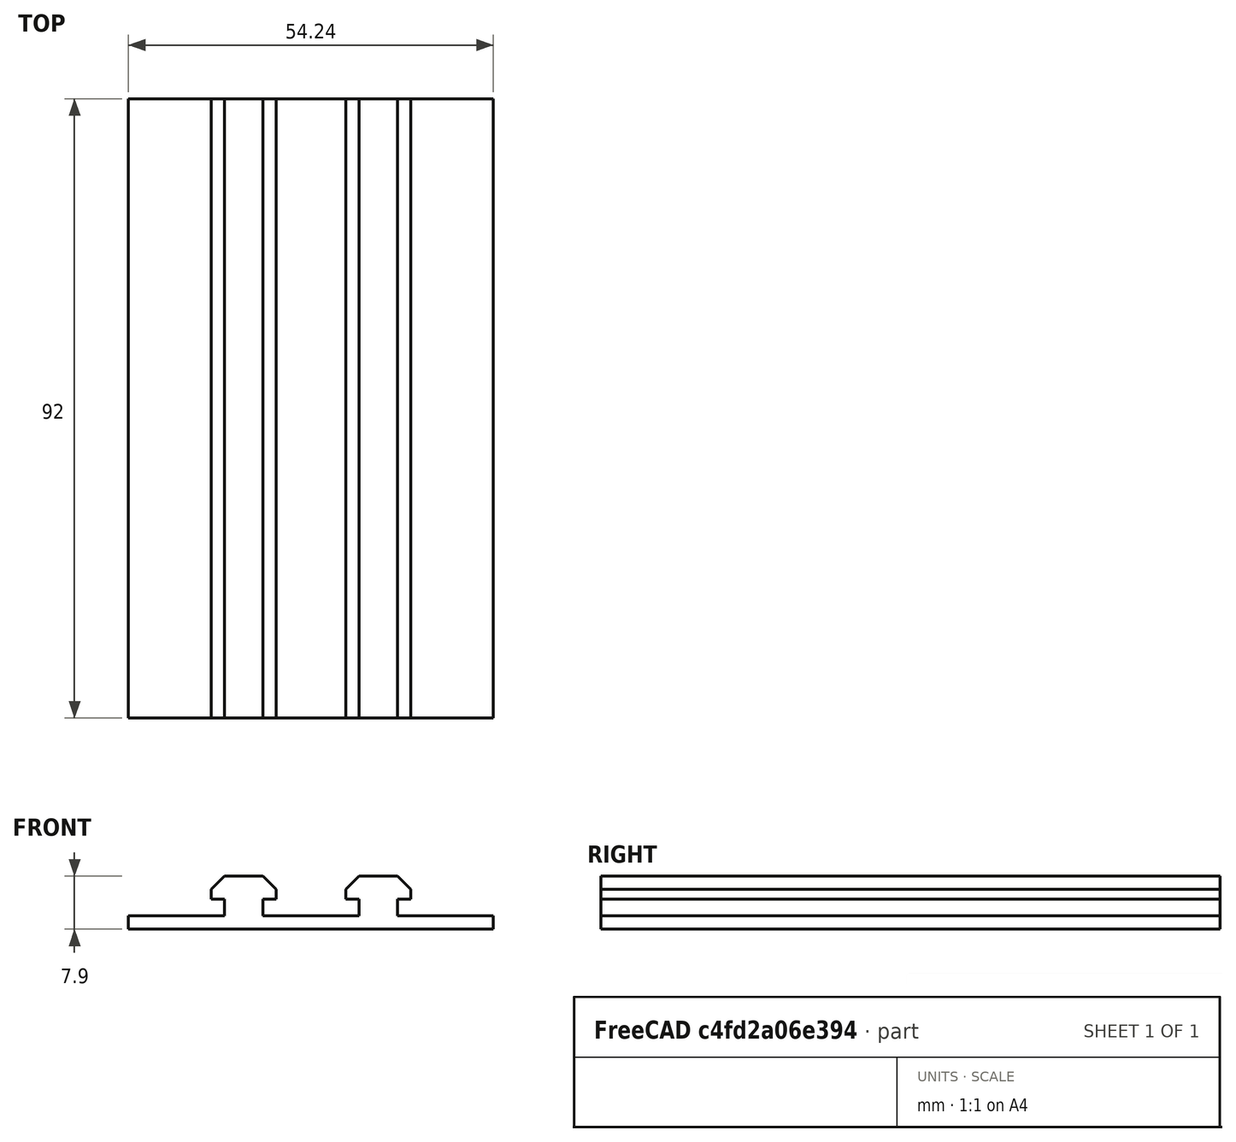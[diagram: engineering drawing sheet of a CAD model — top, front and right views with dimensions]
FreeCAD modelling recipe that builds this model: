
FCSTD DOCUMENT  (FreeCAD 1.0R39109 (Git))
Label: 04 Base Attachment
License: All rights reserved
LicenseURL: https://en.wikipedia.org/wiki/All_rights_reserved
objects: Sketcher::SketchObject×2, PartDesign::Pad×1, PartDesign::Body×1
note: 8 computed .brp shape members not serialized (recipe doc carries the construction recipe); baked Part::Feature solids carry a one-line shape summary decoded from their .brp

FEATURE [Sketcher::SketchObject] Sketch
  ArcFitTolerance = 1e-06
  AttachmentSupport = -> [XZ_Plane]
  FullyConstrained = true
  MakeInternals = false
  MapMode = 5
  Placement = pos=(0,0,0) rot=(1,0,0;1.5708rad)
  sketch-geometry (26):
    g0: LineSegment StartX=-27.12 StartY=0 StartZ=0 EndX=27.12 EndY=0 EndZ=0
    g1: LineSegment StartX=27.12 StartY=0 StartZ=0 EndX=27.12 EndY=2 EndZ=0
    g2: LineSegment StartX=27.12 StartY=2 StartZ=0 EndX=-27.12 EndY=2 EndZ=0
    g3: LineSegment StartX=-27.12 StartY=2 StartZ=0 EndX=-27.12 EndY=0 EndZ=0
    g4: LineSegment StartX=-12.88 StartY=4.5 StartZ=0 EndX=-12.88 EndY=2 EndZ=0
    g5: LineSegment StartX=-12.88 StartY=2 StartZ=0 EndX=-7.12 EndY=2 EndZ=0
    g6: LineSegment StartX=-7.12 StartY=2 StartZ=0 EndX=-7.12 EndY=4.5 EndZ=0
    g7: LineSegment StartX=-7.12 StartY=4.5 StartZ=0 EndX=-12.88 EndY=4.5 EndZ=0
    g8: LineSegment StartX=7.12 StartY=4.5 StartZ=0 EndX=7.12 EndY=2 EndZ=0
    g9: LineSegment StartX=7.12 StartY=2 StartZ=0 EndX=12.88 EndY=2 EndZ=0
    g10: LineSegment StartX=12.88 StartY=2 StartZ=0 EndX=12.88 EndY=4.5 EndZ=0
    g11: LineSegment StartX=12.88 StartY=4.5 StartZ=0 EndX=7.12 EndY=4.5 EndZ=0
    g12: LineSegment StartX=-14.81 StartY=5.93 StartZ=0 EndX=-14.81 EndY=4.5 EndZ=0
    g13: LineSegment StartX=-14.81 StartY=4.5 StartZ=0 EndX=-5.19 EndY=4.5 EndZ=0
    g14: LineSegment StartX=-5.19 StartY=4.5 StartZ=0 EndX=-5.19 EndY=5.93 EndZ=0
    g15: LineSegment StartX=-5.19 StartY=5.93 StartZ=0 EndX=-14.81 EndY=5.93 EndZ=0
    g16: LineSegment StartX=5.19 StartY=4.5 StartZ=0 EndX=14.81 EndY=4.5 EndZ=0
    g17: LineSegment StartX=14.81 StartY=4.5 StartZ=0 EndX=14.81 EndY=5.93 EndZ=0
    g18: LineSegment StartX=14.81 StartY=5.93 StartZ=0 EndX=5.19 EndY=5.93 EndZ=0
    g19: LineSegment StartX=5.19 StartY=5.93 StartZ=0 EndX=5.19 EndY=4.5 EndZ=0
    g20: LineSegment StartX=-14.81 StartY=5.93 StartZ=0 EndX=-12.8442 EndY=7.89576 EndZ=0
    g21: LineSegment StartX=-12.8442 StartY=7.89576 StartZ=0 EndX=-7.15424 EndY=7.89576 EndZ=0
    g22: LineSegment StartX=-7.15424 StartY=7.89576 StartZ=0 EndX=-5.19 EndY=5.93 EndZ=0
    g23: LineSegment StartX=5.19 StartY=5.93 StartZ=0 EndX=7.15576 EndY=7.89576 EndZ=0
    g24: LineSegment StartX=7.15576 StartY=7.89576 StartZ=0 EndX=12.8458 EndY=7.89576 EndZ=0
    g25: LineSegment StartX=12.8458 StartY=7.89576 StartZ=0 EndX=14.81 EndY=5.93 EndZ=0
  constraints (76):
    c: Coincident(g0,g1)
    c: Coincident(g1,g2)
    c: Coincident(g2,g3)
    c: Coincident(g3,g0)
    c: Horizontal(g0)
    c: Horizontal(g2)
    c: Vertical(g1)
    c: Vertical(g3)
    c: Distance(g1,g3) = 54.24
    c: Distance(g0,g2) = 2
    c: DistanceY(g-1,g0) = 0
    c: DistanceX(g0,g-1) = 27.12
    c: Coincident(g4,g5)
    c: Coincident(g5,g6)
    c: Coincident(g6,g7)
    c: Coincident(g7,g4)
    c: Vertical(g4)
    c: Vertical(g6)
    c: Horizontal(g5)
    c: Horizontal(g7)
    c: Distance(g4,g6) = 5.76
    c: Distance(g5,g7) = 2.5
    c: Coincident(g8,g9)
    c: Coincident(g9,g10)
    c: Coincident(g10,g11)
    c: Coincident(g11,g8)
    c: Vertical(g8)
    c: Vertical(g10)
    c: Horizontal(g9)
    c: Horizontal(g11)
    c: Distance(g8,g10) = 5.76
    c: Distance(g9,g11) = 2.5
    c: DistanceY(g2,g4) = 0
    c: DistanceY(g1,g9) = 0
    c: DistanceX(g2,g4) = 14.24
    c: DistanceX(g9,g1) = 14.24
    c: Coincident(g12,g13)
    c: Coincident(g13,g14)
    c: Coincident(g14,g15)
    c: Coincident(g15,g12)
    c: Vertical(g12)
    c: Vertical(g14)
    c: Horizontal(g13)
    c: Horizontal(g15)
    c: Distance(g12,g14) = 9.62
    c: Distance(g13,g15) = 1.43
    c: Coincident(g16,g17)
    c: Coincident(g17,g18)
    c: Coincident(g18,g19)
    c: Coincident(g19,g16)
    c: Horizontal(g16)
    c: Horizontal(g18)
    c: Vertical(g17)
    c: Vertical(g19)
    c: Distance(g17,g19) = 9.62
    c: Distance(g16,g18) = 1.43
    c: DistanceY(g4,g12) = 0
    c: DistanceY(g10,g16) = 0
    c: DistanceX(g12,g4) = 1.93
    c: DistanceX(g10,g16) = 1.93
    c: Distance(g20) = 2.78
    c: Angle(g-1,g20) = 0.785398
    c: Coincident(g20,g12)
    c: Distance(g21) = 5.69
    c: Coincident(g21,g20)
    c: Horizontal(g21)
    c: Coincident(g22,g21)
    c: Coincident(g22,g14)
    c: Distance(g23) = 2.78
    c: Angle(g-1,g23) = 0.785398
    c: Coincident(g23,g18)
    c: Distance(g24) = 5.69
    c: Coincident(g24,g23)
    c: Horizontal(g24)
    c: Coincident(g25,g24)
    c: Coincident(g25,g17)
FEATURE [Sketcher::SketchObject] Sketch001
  ArcFitTolerance = 1e-06
  AttachmentSupport = -> [XZ_Plane]
  FullyConstrained = true
  MakeInternals = false
  MapMode = 5
  Placement = pos=(0,0,0) rot=(1,0,0;1.5708rad)
  sketch-geometry (24):
    g0: LineSegment StartX=-27.12 StartY=0 StartZ=0 EndX=27.12 EndY=0 EndZ=0
    g1: LineSegment StartX=27.12 StartY=0 StartZ=0 EndX=27.12 EndY=2 EndZ=0
    g2: LineSegment StartX=27.12 StartY=2 StartZ=0 EndX=12.88 EndY=2 EndZ=0
    g3: LineSegment StartX=12.88 StartY=2 StartZ=0 EndX=12.88 EndY=4.5 EndZ=0
    g4: LineSegment StartX=12.88 StartY=4.5 StartZ=0 EndX=14.81 EndY=4.5 EndZ=0
    g5: LineSegment StartX=14.81 StartY=4.5 StartZ=0 EndX=14.81 EndY=5.93 EndZ=0
    g6: LineSegment StartX=14.81 StartY=5.93 StartZ=0 EndX=12.8442 EndY=7.89576 EndZ=0
    g7: LineSegment StartX=12.8442 StartY=7.89576 StartZ=0 EndX=7.15424 EndY=7.89576 EndZ=0
    g8: LineSegment StartX=7.15424 StartY=7.89576 StartZ=0 EndX=5.18849 EndY=5.93 EndZ=0
    g9: LineSegment StartX=5.18849 StartY=5.93 StartZ=0 EndX=5.18849 EndY=4.5 EndZ=0
    g10: LineSegment StartX=5.18849 StartY=4.5 StartZ=0 EndX=7.11849 EndY=4.5 EndZ=0
    g11: LineSegment StartX=7.11849 StartY=4.5 StartZ=0 EndX=7.11849 EndY=2 EndZ=0
    g12: LineSegment StartX=7.11849 StartY=2 StartZ=0 EndX=-7.12151 EndY=2 EndZ=0
    g13: LineSegment StartX=-7.12151 StartY=2 StartZ=0 EndX=-7.12151 EndY=4.5 EndZ=0
    g14: LineSegment StartX=-7.12151 StartY=4.5 StartZ=0 EndX=-5.19151 EndY=4.5 EndZ=0
    g15: LineSegment StartX=-5.19151 StartY=4.5 StartZ=0 EndX=-5.19151 EndY=5.93 EndZ=0
    g16: LineSegment StartX=-5.19151 StartY=5.93 StartZ=0 EndX=-7.15576 EndY=7.89727 EndZ=0
    g17: LineSegment StartX=-7.15576 StartY=7.89727 StartZ=0 EndX=-12.8458 EndY=7.89727 EndZ=0
    g18: LineSegment StartX=-12.8458 StartY=7.89727 StartZ=0 EndX=-14.81 EndY=5.93 EndZ=0
    g19: LineSegment StartX=-14.81 StartY=5.93 StartZ=0 EndX=-14.81 EndY=4.5 EndZ=0
    g20: LineSegment StartX=-14.81 StartY=4.5 StartZ=0 EndX=-12.88 EndY=4.5 EndZ=0
    g21: LineSegment StartX=-12.88 StartY=4.5 StartZ=0 EndX=-12.88 EndY=2 EndZ=0
    g22: LineSegment StartX=-12.88 StartY=2 StartZ=0 EndX=-27.12 EndY=2 EndZ=0
    g23: LineSegment StartX=-27.12 StartY=2 StartZ=0 EndX=-27.12 EndY=0 EndZ=0
  constraints (72):
    c: Horizontal(g0)
    c: Coincident(g0,g1)
    c: Coincident(g1,g2)
    c: Horizontal(g2)
    c: Coincident(g2,g3)
    c: Vertical(g3)
    c: Coincident(g3,g4)
    c: Coincident(g4,g5)
    c: Vertical(g5)
    c: Coincident(g5,g6)
    c: Coincident(g6,g7)
    c: Coincident(g7,g8)
    c: Coincident(g8,g9)
    c: Vertical(g9)
    c: Coincident(g9,g10)
    c: Coincident(g10,g11)
    c: Coincident(g11,g12)
    c: Horizontal(g12)
    c: Coincident(g12,g13)
    c: Vertical(g13)
    c: Coincident(g13,g14)
    c: Coincident(g14,g15)
    c: Coincident(g15,g16)
    c: Coincident(g16,g17)
    c: Coincident(g17,g18)
    c: Coincident(g18,g19)
    c: Vertical(g19)
    c: Coincident(g19,g20)
    c: Coincident(g20,g21)
    c: Coincident(g21,g22)
    c: Horizontal(g22)
    c: Coincident(g22,g23)
    c: Coincident(g23,g0)
    c: Vertical(g23)
    c: Horizontal(g17)
    c: Horizontal(g20,g19)
    c: Horizontal(g14)
    c: Horizontal(g4)
    c: Horizontal(g7)
    c: Horizontal(g10)
    c: Vertical(g21)
    c: Vertical(g11)
    c: Vertical(g1)
    c: Distance(g0) = 54.24
    c: Distance(g22) = 14.24
    c: Distance(g23) = 2
    c: Distance(g1) = 2
    c: DistanceY(g-1,g0) = 0
    c: DistanceY(g-1,g12) = 2
    c: DistanceX(g0,g-1) = 27.12
    c: Distance(g21) = 2.5
    c: Distance(g13) = 2.5
    c: Distance(g11) = 2.5
    c: Distance(g3) = 2.5
    c: Distance(g12) = 14.24
    c: Distance(g20) = 1.93
    c: Distance(g14) = 1.93
    c: Distance(g2) = 14.24
    c: Vertical(g15)
    c: Distance(g10) = 1.93
    c: Distance(g4) = 1.93
    c: Distance(g19) = 1.43
    c: Distance(g15) = 1.43
    c: Distance(g9) = 1.43
    c: Distance(g5) = 1.43
    c: Distance(g6) = 2.78
    c: Distance(g8) = 2.78
    c: Distance(g16) = 2.78
    c: Distance(g18) = 2.78
    c: Distance(g17) = 5.69
    c: Distance(g7) = 5.69
    c: Angle(g8,g0) = 2.35619
FEATURE [PartDesign::Pad] Pad
  Direction = (0,-1,2e-16)
  Length = 92
  Length2 = 10
  Placement = pos=(0,0,0) rot=(1,0,0;1.5708rad)
  Profile = -> Sketch001
  ReferenceAxis = -> Sketch001 [N_Axis]
  Refine = true
  Suppressed = false
  Type = 0
FEATURE [PartDesign::Body] Body
  AllowCompound = false
  Group = -> [Sketch,Sketch001,Pad]
  Origin = -> Origin
  Tip = -> Pad
